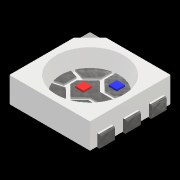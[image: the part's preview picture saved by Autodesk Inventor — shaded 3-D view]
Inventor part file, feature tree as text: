
AUTODESK INVENTOR PART (.ipt)
format: ipt  version: 2017 SP1 (Build 210196100, 196)  size: 312,320 bytes
history: native  units: mm
features: other x4, extrude x2, sketch x2, projected_geometry x2
ambient origin geometry x8: Origin, YZ Plane, XZ Plane, XY Plane, X Axis, Y Axis, Z Axis, Center Point
bodies: Body1 (feature_tree)
feature tree (10):
  other  "LED SMD 5050.ipt"
  extrude  "Выдавливание1"  Depth=10.0mm
  extrude  "Выдавливание2"  Depth=0.2mm
  other  "Твердое тело1::LED SMD 5050.ipt"
  other  "Элемент создания тегов1"
  sketch  "Эскиз1"
  sketch  "Эскиз2"
  projected_geometry  "Спроецированная петля1"
  projected_geometry  "Спроецированная петля2"
  other  "Твердое тело1"
